# Revit family: 3-668-xx - 37-668-xx - Ellipse (Pendant)
name_source: partatom
category: Lighting Fixtures
revit_build: Autodesk Revit 2018 (Build: 20170223_1515(x64)
units: mm (PartAtom-declared; Revit-internal decimal feet)

## family parameters
Always vertical = Yes
Cut with Voids When Loaded = No
Host = Ceiling
Light Source = Yes
OmniClass Number = 23.80.70.11
OmniClass Title = Luminaries for Internal Lighting
Part Type = Normal
Room Calculation Point = No
Round Connector Dimension = Use Diameter
Shared = No

## types (12) — shared parameters
Color Filter = 16777215
Dimming Lamp Color Temperature Shift = <None>
Emit Shape Visible in Rendering = No
Emit from Circle Diameter = 2 "
Lamp = LED Array
Manufacturer = Oxygen Lighting & Fans
Model = 3-668-XX / 37-668-XX - Ellipse
Other 1 = Braided Cord
Supplied with = Supplied with 8 ft of braided cord
Tilt Angle = 90.00°
URL = www.oxygenlighting.com
Wattage Comments = 7.09 W at 120 V

## per-type parameters (varying)
| type | Main Diffuser | Metal Finish | Photometric Web File | Voltage |
| 3-668-115 - Black / White Opal Glass | White Opal Glass | 15 - Black | 3-668-124 Ellipse Pendant with Glass Enclosure.ies | 120 V |
| 3-668-215 - Black / Matte White Acrylic | Matte White Acrylic | 15 - Black | 3-668-220 Ellipse Pendant with Acrylic Enclosure.ies | 120 V |
| 3-668-120 - Polished Nickel / White Opal Glass | White Opal Glass | 20 - Polished Nickel | 3-668-124 Ellipse Pendant with Glass Enclosure.ies | 120 V |
| 3-668-124 - Satin Nickel / White Opal Glass | White Opal Glass | 24 - Satin Nickel | 3-668-124 Ellipse Pendant with Glass Enclosure.ies | 120 V |
| 3-668-224 - Satin Nickel / Matte White Acrylic | Matte White Acrylic | 24 - Satin Nickel | 3-668-220 Ellipse Pendant with Acrylic Enclosure.ies | 120 V |
| 3-668-220 - Polished Nickel / Matte White Acrylic | Matte White Acrylic | 20 - Polished Nickel | 3-668-220 Ellipse Pendant with Acrylic Enclosure.ies | 120 V |
| 37-668-115 - Black / White Opal Glass | White Opal Glass | 15 - Black | 3-668-124 Ellipse Pendant with Glass Enclosure.ies | 277 V |
| 37-668-120 - Polished Nickel / White Opal Glass | White Opal Glass | 20 - Polished Nickel | 3-668-124 Ellipse Pendant with Glass Enclosure.ies | 277 V |
| 37-668-124 - Satin Nickel / White Opal Glass | White Opal Glass | 24 - Satin Nickel | 3-668-124 Ellipse Pendant with Glass Enclosure.ies | 277 V |
| 37-668-215 - Black / Matte White Acrylic | Matte White Acrylic | 15 - Black | 3-668-220 Ellipse Pendant with Acrylic Enclosure.ies | 277 V |
| 37-668-220 - Polished Nickel / Matte White Acrylic | Matte White Acrylic | 20 - Polished Nickel | 3-668-220 Ellipse Pendant with Acrylic Enclosure.ies | 277 V |
| 37-668-224 - Satin Nickel / Matte White Acrylic | Matte White Acrylic | 24 - Satin Nickel | 3-668-220 Ellipse Pendant with Acrylic Enclosure.ies | 277 V |

## geometry (parser evidence)
native form markers: Sweep x7
no freeform markers — native parametric forms only
